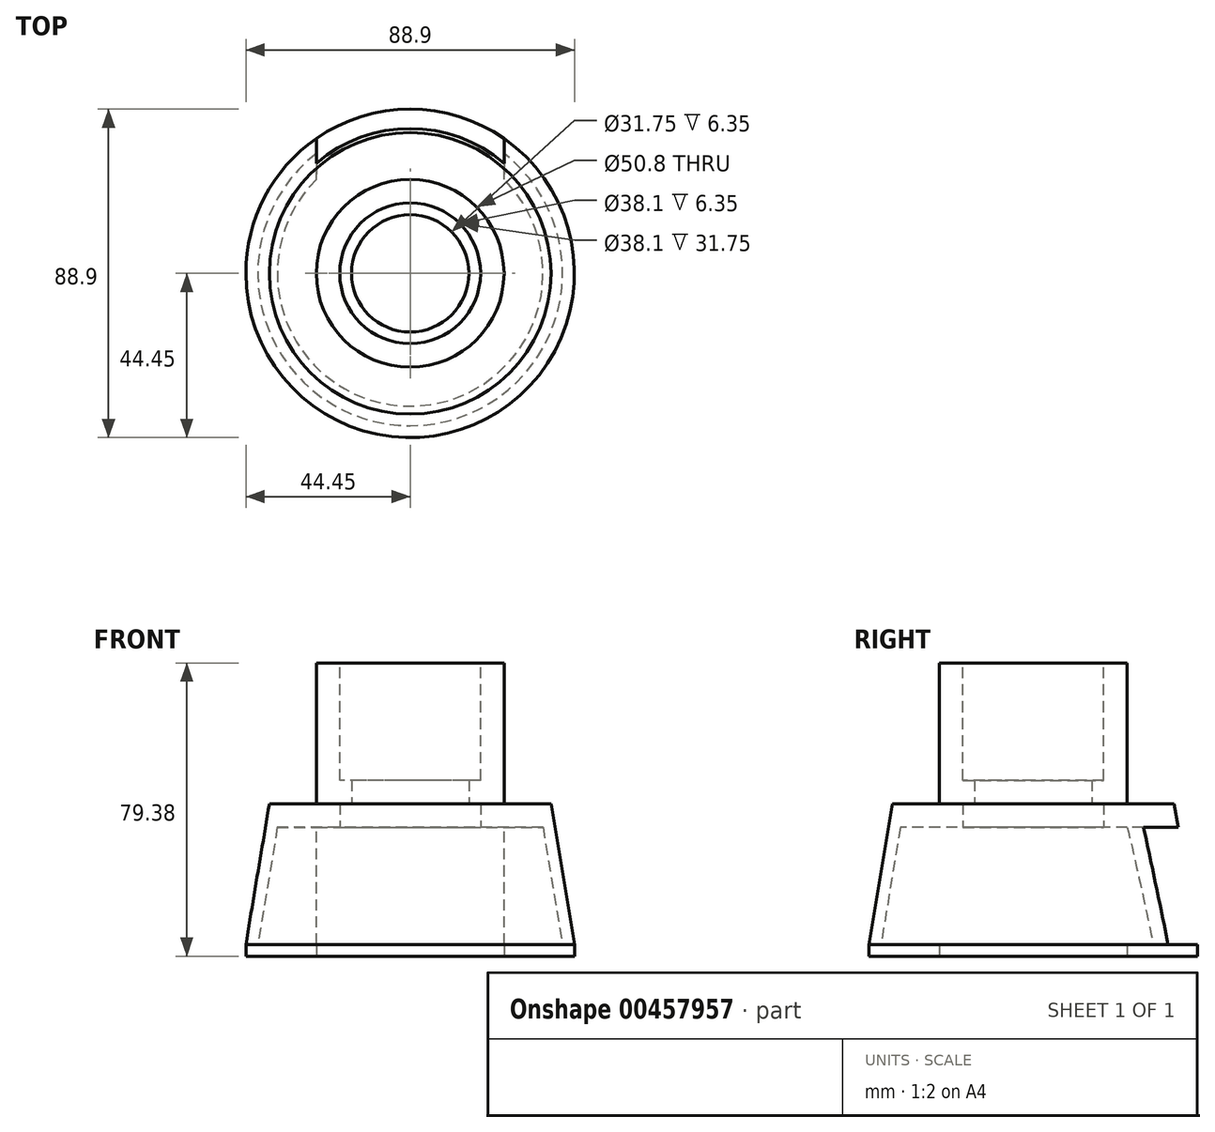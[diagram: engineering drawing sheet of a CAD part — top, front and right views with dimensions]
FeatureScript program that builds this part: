
annotation { "Feature Type Name" : "Feature", "Feature Type Description" : "" }
export const myFeature = defineFeature(function(context is Context, id is Id, definition is map)
    precondition{}
    {
        {
            var Q0;
            Q0=qCreatedBy(makeId("Front.planeOp"),FACE);
            var sketch = newSketch(context, id + "F0", { "sketchPlane" : qUnion([Q0])});
            skLineSegment(sketch, "E0", {"start": v(0, 0) * mm, "end": v(0, 385.96) * mm, "construction": true});
            skLineSegment(sketch, "E1", {"start": v(-44.45, 0) * mm, "end": v(-38.1, 38.1) * mm});
            skLineSegment(sketch, "E2", {"start": v(-38.1, 38.1) * mm, "end": v(-25.4, 38.1) * mm});
            skLineSegment(sketch, "E3", {"start": v(-25.4, 38.1) * mm, "end": v(-25.4, 76.2) * mm});
            skLineSegment(sketch, "E4", {"start": v(-25.4, 76.2) * mm, "end": v(-15.87, 76.2) * mm});
            skLineSegment(sketch, "E5", {"start": v(-15.87, 76.2) * mm, "end": v(-15.87, 38.1) * mm});
            skLineSegment(sketch, "E6", {"start": v(-15.87, 38.1) * mm, "end": v(-19.05, 38.1) * mm});
            skLineSegment(sketch, "E7", {"start": v(-19.05, 38.1) * mm, "end": v(-19.05, 31.75) * mm});
            skLineSegment(sketch, "E8", {"start": v(-19.05, 31.75) * mm, "end": v(-35.94, 31.75) * mm});
            skLineSegment(sketch, "E9", {"start": v(-35.94, 31.75) * mm, "end": v(-41.23, 0) * mm});
            skLineSegment(sketch, "E10", {"start": v(-44.45, -3.18) * mm, "end": v(-44.45, 0) * mm});
            skLineSegment(sketch, "E11", {"start": v(-41.23, 0) * mm, "end": v(-25.4, 0) * mm});
            skLineSegment(sketch, "E12", {"start": v(-25.4, 0) * mm, "end": v(-25.4, -3.18) * mm});
            skLineSegment(sketch, "E13", {"start": v(-25.4, -3.18) * mm, "end": v(-44.45, -3.18) * mm});
            skSolve(sketch);
        }
        {
            var Q0;
            Q0=qSketchRegion(id+"F0",true);
            var Q1;
            Q1=sQuery(id+"F0.wireOp",EDGE,"E0");
            revolve(context, id + "F1", {"entities" : qUnion([Q0]), "axis" : qUnion([Q1]), "revolveType" : RevolveType.FULL});
        }
        {
            var Q0;
            Q0=qCreatedBy(makeId("Front.planeOp"),FACE);
            var sketch = newSketch(context, id + "F2", { "sketchPlane" : qUnion([Q0])});
            skLineSegment(sketch, "E14.bottom", {"start": v(-25.4, 31.75) * mm, "end": v(25.4, 31.75) * mm});
            skLineSegment(sketch, "E14.top", {"start": v(-25.4, 0) * mm, "end": v(25.4, 0) * mm});
            skLineSegment(sketch, "E14.left", {"start": v(-25.4, 31.75) * mm, "end": v(-25.4, 0) * mm});
            skLineSegment(sketch, "E14.right", {"start": v(25.4, 31.75) * mm, "end": v(25.4, 0) * mm});
            skLineSegment(sketch, "E15.bottom", {"start": v(-25.4, 0) * mm, "end": v(-25.71, 5.44) * mm});
            skSolve(sketch);
        }
        {
            var Q0;
            Q0=qSketchRegion(id+"F2",true);
            extrude(context, id + "F3", {"entities" : qUnion([Q0]), "operationType" : NewBodyOperationType.REMOVE, "endBound" : BoundingType.THROUGH_ALL, "oppositeDirection" : true, "depth" : 25.4 * mm});
        }
        {
            var Q0;
            Q0=makeQuery(id+"F1.opRevolve","SWEPT_FACE",FACE,{"disambiguationData":[OSD([sQuery(id+"F0.wireOp",EDGE,"E4")])]});
            var sketch = newSketch(context, id + "F4", { "sketchPlane" : qUnion([Q0])});
            skCircle(sketch, "E16", {"center": v(0, 0) * mm, "radius": 19.05 * mm});
            skSolve(sketch);
        }
        {
            var Q0;
            Q0 = qSketchRegion(id + "F4", true);
            extrude(context, id + "F5", {"entities" : qUnion([Q0]), "operationType" : NewBodyOperationType.REMOVE, "oppositeDirection" : true, "depth" : 31.75 * mm});
        }
    });
